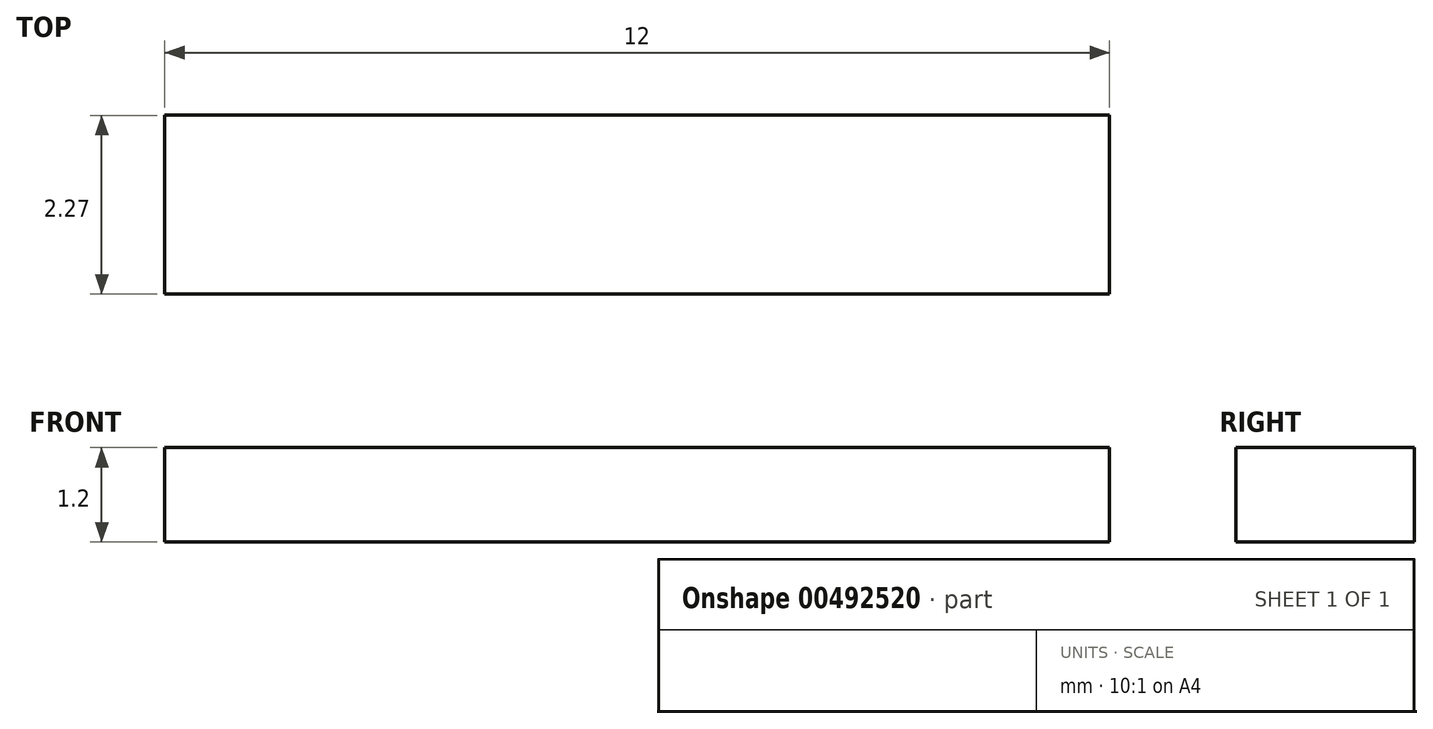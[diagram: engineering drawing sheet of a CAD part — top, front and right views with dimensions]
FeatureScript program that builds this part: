
annotation { "Feature Type Name" : "Feature", "Feature Type Description" : "" }
export const myFeature = defineFeature(function(context is Context, id is Id, definition is map)
    precondition{}
    {
        {
            var Q0;
            Q0=qCreatedBy(makeId("Top.planeOp"),FACE);
            var sketch = newSketch(context, id + "F0", { "sketchPlane" : qUnion([Q0])});
            skLineSegment(sketch, "E0.bottom", {"start": v(-46.56, 13.18) * mm, "end": v(-34.56, 13.18) * mm});
            skLineSegment(sketch, "E0.top", {"start": v(-46.56, 10.91) * mm, "end": v(-34.56, 10.91) * mm});
            skLineSegment(sketch, "E0.left", {"start": v(-46.56, 13.18) * mm, "end": v(-46.56, 10.91) * mm});
            skLineSegment(sketch, "E0.right", {"start": v(-34.56, 13.18) * mm, "end": v(-34.56, 10.91) * mm});
            skSolve(sketch);
        }
        {
            var Q0;
            Q0=makeQuery(id+"F0.imprint","IMPRINT",FACE,{"disambiguationData":[TD([[makeQuery(id+"F0.imprint","IMPRINT",EDGE,{"derivedFrom":sQuery(id+"F0.wireOp",EDGE,"E0.bottom")}),-1.0]])]});
            extrude(context, id + "F1", {"entities" : qUnion([Q0]), "depth" : 1.2 * mm});
        }
    });
